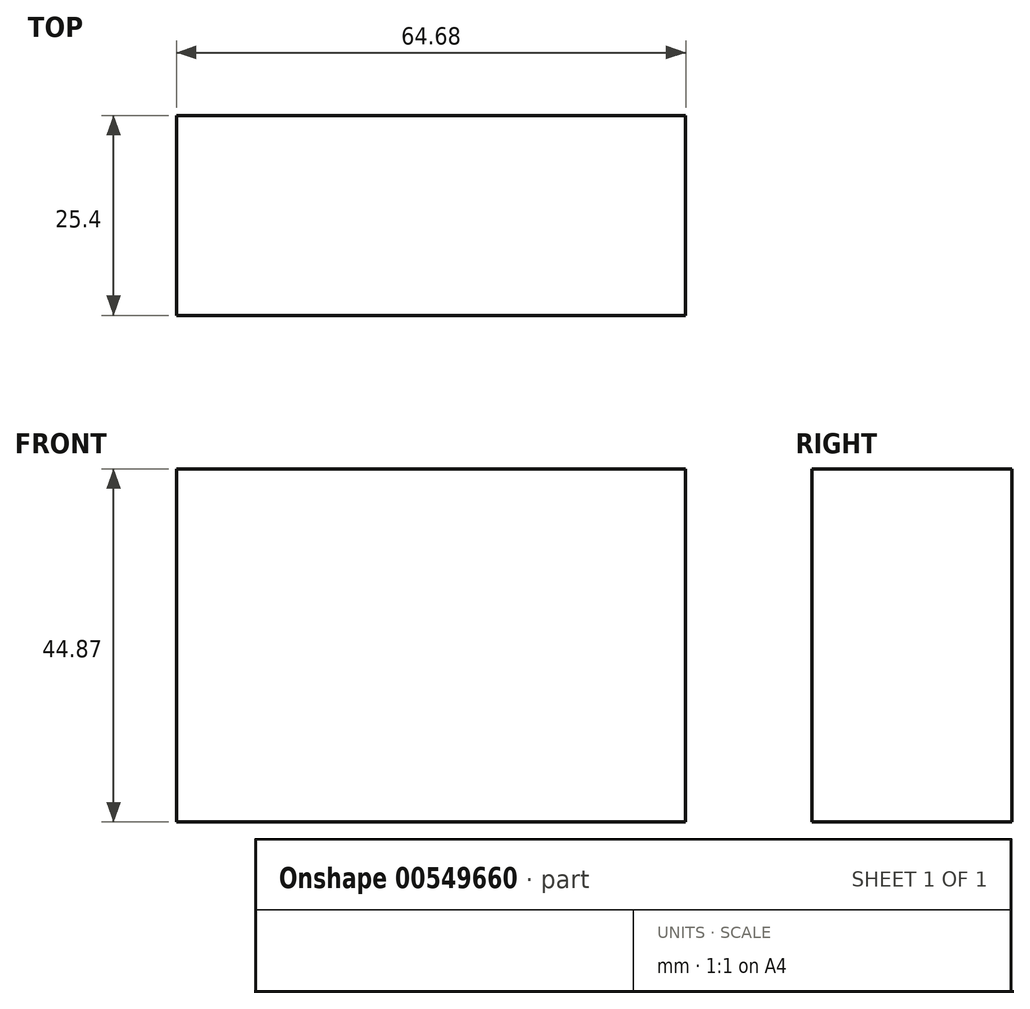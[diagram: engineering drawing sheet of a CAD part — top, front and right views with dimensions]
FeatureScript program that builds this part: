
annotation { "Feature Type Name" : "Feature", "Feature Type Description" : "" }
export const myFeature = defineFeature(function(context is Context, id is Id, definition is map)
    precondition{}
    {
        {
            var Q0;
            Q0=qCreatedBy(makeId("Front.planeOp"),FACE);
            var sketch = newSketch(context, id + "F0", { "sketchPlane" : qUnion([Q0])});
            skLineSegment(sketch, "E0.bottom", {"start": v(-114.04, 71.93) * mm, "end": v(-49.36, 71.93) * mm});
            skLineSegment(sketch, "E0.top", {"start": v(-114.04, 27.06) * mm, "end": v(-49.36, 27.06) * mm});
            skLineSegment(sketch, "E0.left", {"start": v(-114.04, 71.93) * mm, "end": v(-114.04, 27.06) * mm});
            skLineSegment(sketch, "E0.right", {"start": v(-49.36, 71.93) * mm, "end": v(-49.36, 27.06) * mm});
            skSolve(sketch);
        }
        {
            var Q0;
            Q0 = qSketchRegion(id + "F0", true);
            extrude(context, id + "F1", {"entities" : qUnion([Q0]), "depth" : 25.4 * mm, "offsetDistance" : 25.4 * mm});
        }
        {
            var Q0;
            Q0=qCreatedBy(makeId("Front.planeOp"),FACE);
            var sketch = newSketch(context, id + "F2", { "sketchPlane" : qUnion([Q0])});
            skFitSpline(sketch, "E1", {"points": [v(-3.17, 53.2) * mm, v(30.89, 53.2) * mm, v(42.24, 44.74) * mm, v(73.65, 29.43) * mm, v(90.8, 26.27) * mm, v(128.3, 34.98) * mm, v(133.57, 39.46) * mm, v(133.3, 48.44) * mm], "startDerivative": vector(218.32, 20.84) * mm, "endDerivative": vector(-14.05, 106.03) * mm});
            skSolve(sketch);
        }
        {
            var Q0;
            Q0=sQuery(id+"F2.wireOp",EDGE,"E1");
            extrude(context, id + "F3", {"bodyType" : ToolBodyType.SURFACE, "surfaceEntities" : qUnion([Q0]), "depth" : 43.94 * mm, "offsetDistance" : 25.4 * mm});
        }
    });
